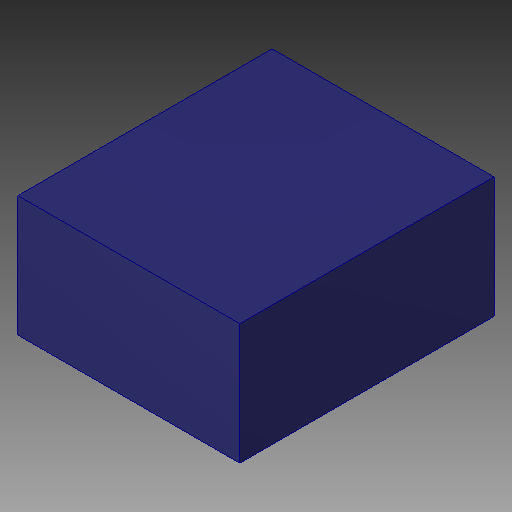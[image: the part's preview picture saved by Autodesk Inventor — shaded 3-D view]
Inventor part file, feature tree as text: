
AUTODESK INVENTOR PART (.ipt)
format: ipt  version: 2019 (Build 230136000, 136)  size: 89,088 bytes
history: native  units: in
note: dims shown in document units (in); Inventor stores cm internally (conversion verified against a paired STEP export)
features: extrude x1, other x1
ambient origin geometry x8: Origin, YZ Plane, XZ Plane, XY Plane, X Axis, Y Axis, Z Axis, Center Point
bodies: Solid1 (feature_tree)
feature tree (2):
  extrude  "Extrusion1"  Depth=0.4547in TaperAngle=0.0deg
  other  "SHDR3W54P0X254_1X3_953X483X115_11.550000, 3296W-1-103LF_11.550000_1"
